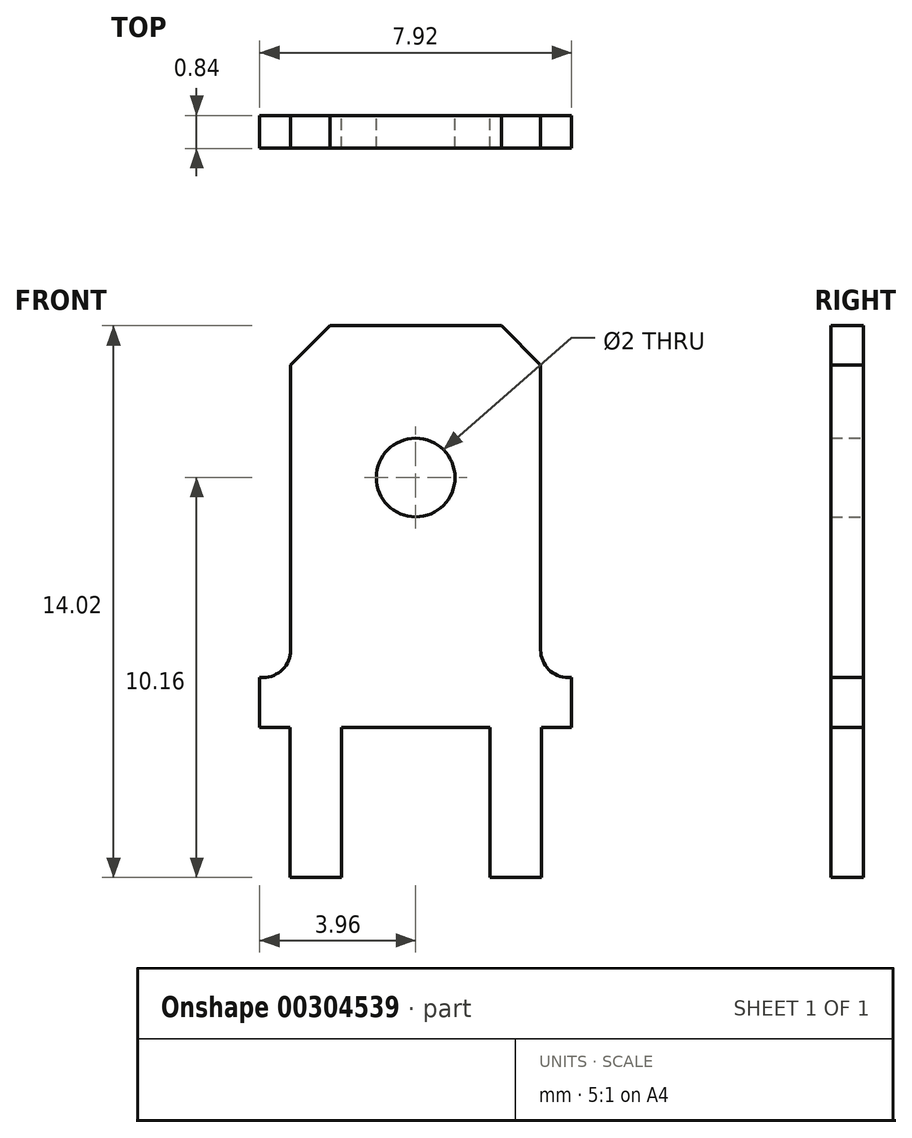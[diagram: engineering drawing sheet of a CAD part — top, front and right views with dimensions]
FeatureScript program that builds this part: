
annotation { "Feature Type Name" : "Feature", "Feature Type Description" : "" }
export const myFeature = defineFeature(function(context is Context, id is Id, definition is map)
    precondition{}
    {
        {
            var Q0;
            Q0=qCreatedBy(makeId("Front.planeOp"),FACE);
            var sketch = newSketch(context, id + "F0", { "sketchPlane" : qUnion([Q0])});
            skLineSegment(sketch, "E0", {"start": v(-3.96, 0) * mm, "end": v(-3.96, 1.27) * mm});
            skLineSegment(sketch, "E1", {"start": v(-3.96, 1.27) * mm, "end": v(-3.17, 1.27) * mm});
            skLineSegment(sketch, "E2", {"start": v(-3.17, 1.27) * mm, "end": v(-3.17, 10.2) * mm});
            skLineSegment(sketch, "E3", {"start": v(-3.17, 10.2) * mm, "end": v(3.18, 10.2) * mm});
            skLineSegment(sketch, "E4", {"start": v(3.18, 10.2) * mm, "end": v(3.18, 1.27) * mm});
            skLineSegment(sketch, "E5", {"start": v(3.18, 1.27) * mm, "end": v(3.96, 1.27) * mm});
            skLineSegment(sketch, "E6", {"start": v(3.96, 1.27) * mm, "end": v(3.96, 0) * mm});
            skLineSegment(sketch, "E7", {"start": v(3.96, 0) * mm, "end": v(3.2, 0) * mm});
            skLineSegment(sketch, "E8", {"start": v(3.2, 0) * mm, "end": v(3.2, -3.81) * mm});
            skLineSegment(sketch, "E9", {"start": v(3.2, -3.81) * mm, "end": v(1.88, -3.81) * mm});
            skLineSegment(sketch, "E10", {"start": v(1.89, -3.81) * mm, "end": v(1.89, 0) * mm});
            skLineSegment(sketch, "E11", {"start": v(1.89, 0) * mm, "end": v(-1.88, 0) * mm});
            skLineSegment(sketch, "E12", {"start": v(-1.88, 0) * mm, "end": v(-1.88, -3.81) * mm});
            skLineSegment(sketch, "E13", {"start": v(-1.88, -3.81) * mm, "end": v(-3.2, -3.81) * mm});
            skLineSegment(sketch, "E14", {"start": v(-3.2, -3.81) * mm, "end": v(-3.2, 0) * mm});
            skLineSegment(sketch, "E15", {"start": v(-3.2, 0) * mm, "end": v(-3.96, 0) * mm});
            skPoint(sketch, "E16", {"position": v(0, 10.2) * mm});
            skPoint(sketch, "E17", {"position": v(0, 0) * mm});
            skLineSegment(sketch, "E18", {"start": v(-2.54, -3.81) * mm, "end": v(-2.54, 3.41) * mm, "construction": true});
            skLineSegment(sketch, "E19", {"start": v(2.54, -3.81) * mm, "end": v(2.54, 3.41) * mm, "construction": true});
            skCircle(sketch, "E20", {"center": v(0, 6.35) * mm, "radius": 1 * mm});
            skSolve(sketch);
        }
        {
            var Q0;
            Q0 = qSketchRegion(id + "F0", true);
            extrude(context, id + "F1", {"entities" : qUnion([Q0]), "endBound" : BoundingType.SYMMETRIC, "depth" : .83 * mm});
        }
        {
            var Q0;
            Q0=makeQuery(id+"F1.opExtrude","SWEPT_EDGE",EDGE,{"disambiguationData":[OSD([sQuery(id+"F0.wireOp",EDGE,"E3"),sQuery(id+"F0.wireOp",EDGE,"E4")])]});
            var Q1;
            Q1=makeQuery(id+"F1.opExtrude","SWEPT_EDGE",EDGE,{"disambiguationData":[OSD([sQuery(id+"F0.wireOp",EDGE,"E2"),sQuery(id+"F0.wireOp",EDGE,"E3")])]});
            chamfer(context, id + "F2", {"entities" : qUnion([Q0, Q1]), "width" : 1 * mm, "tangentPropagation" : true});
        }
        {
            var Q0;
            Q0=makeQuery(id+"F1.opExtrude","SWEPT_EDGE",EDGE,{"disambiguationData":[OSD([sQuery(id+"F0.wireOp",EDGE,"E4"),sQuery(id+"F0.wireOp",EDGE,"E5")])]});
            var Q1;
            Q1=makeQuery(id+"F1.opExtrude","SWEPT_EDGE",EDGE,{"disambiguationData":[OSD([sQuery(id+"F0.wireOp",EDGE,"E1"),sQuery(id+"F0.wireOp",EDGE,"E2")])]});
            fillet(context, id + "F3", {"entities" : qUnion([Q0, Q1]), "radius" : .7 * mm, "tangentPropagation" : true, "allowEdgeOverflow" : false});
        }
    });
